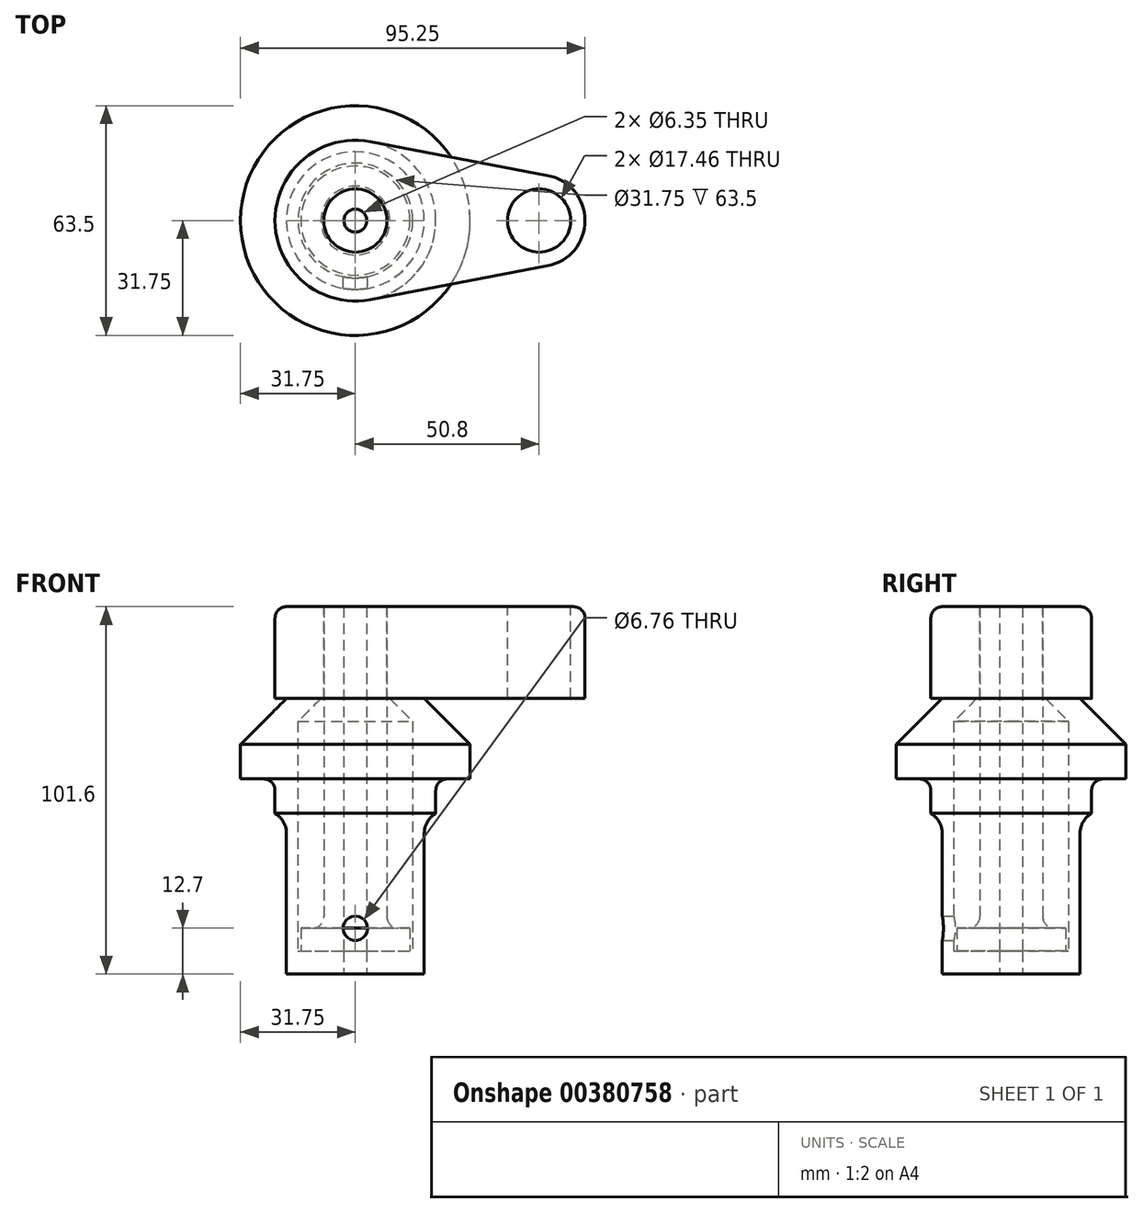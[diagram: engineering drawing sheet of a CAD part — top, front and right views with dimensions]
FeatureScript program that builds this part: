
annotation { "Feature Type Name" : "Feature", "Feature Type Description" : "" }
export const myFeature = defineFeature(function(context is Context, id is Id, definition is map)
    precondition{}
    {
        {
            var Q0;
            Q0=qCreatedBy(makeId("Front.planeOp"),FACE);
            var sketch = newSketch(context, id + "F0", { "sketchPlane" : qUnion([Q0])});
            skLineSegment(sketch, "E0", {"start": v(0, 0) * mm, "end": v(0, 76.2) * mm});
            skLineSegment(sketch, "E1", {"start": v(0, 76.2) * mm, "end": v(19.05, 76.2) * mm});
            skLineSegment(sketch, "E2", {"start": v(19.05, 76.2) * mm, "end": v(31.75, 63.5) * mm});
            skLineSegment(sketch, "E3", {"start": v(31.75, 63.5) * mm, "end": v(31.75, 53.98) * mm});
            skLineSegment(sketch, "E4", {"start": v(31.75, 53.98) * mm, "end": v(22.23, 53.98) * mm});
            skLineSegment(sketch, "E5", {"start": v(22.23, 53.98) * mm, "end": v(22.23, 44.45) * mm});
            skLineSegment(sketch, "E6", {"start": v(22.23, 44.45) * mm, "end": v(19.05, 44.45) * mm});
            skLineSegment(sketch, "E7", {"start": v(19.05, 44.45) * mm, "end": v(19.05, 0) * mm});
            skLineSegment(sketch, "E8", {"start": v(19.05, 0) * mm, "end": v(0, 0) * mm});
            skLineSegment(sketch, "E9", {"start": v(0, 6.35) * mm, "end": v(15.88, 6.35) * mm});
            skLineSegment(sketch, "E10", {"start": v(15.88, 6.35) * mm, "end": v(15.88, 69.85) * mm});
            skLineSegment(sketch, "E11", {"start": v(15.88, 69.85) * mm, "end": v(9.52, 76.2) * mm});
            skLineSegment(sketch, "E12", {"start": v(0, 76.2) * mm, "end": v(0, 87.9) * mm, "construction": true});
            skLineSegment(sketch, "E13", {"start": v(0, 76.2) * mm, "end": v(0, 101.6) * mm});
            skLineSegment(sketch, "E14", {"start": v(0, 101.6) * mm, "end": v(8.73, 101.6) * mm});
            skLineSegment(sketch, "E15", {"start": v(8.73, 101.6) * mm, "end": v(8.73, 12.7) * mm});
            skLineSegment(sketch, "E16", {"start": v(8.73, 12.7) * mm, "end": v(15.08, 12.7) * mm});
            skLineSegment(sketch, "E17", {"start": v(15.08, 12.7) * mm, "end": v(15.08, 6.35) * mm});
            skSolve(sketch);
        }
        {
            var Q0;
            {var subQ3=sQuery(id+"F0.wireOp",EDGE,"E2");Q0=makeQuery(id+"F0.imprint","IMPRINT",FACE,{"disambiguationData":[TD([[makeQuery(id+"F0.imprint","IMPRINT",EDGE,{"derivedFrom":subQ3}),-1.0]])]});}
            var Q1;
            Q1=sQuery(id+"F0.wireOp",EDGE,"E0");
            revolve(context, id + "F1", {"entities" : qUnion([Q0]), "axis" : qUnion([Q1]), "revolveType" : RevolveType.FULL});
        }
        {
            var Q0;
            {var subQ0=sQuery(id+"F0.wireOp",EDGE,"E13");Q0=makeQuery(id+"F0.imprint","IMPRINT",FACE,{"disambiguationData":[TD([[makeQuery(id+"F0.imprint","IMPRINT",EDGE,{"derivedFrom":subQ0}),-1.0]])]});}
            var Q1;
            {var subQ0=sQuery(id+"F0.wireOp",EDGE,"E16");Q1=makeQuery(id+"F0.imprint","IMPRINT",FACE,{"disambiguationData":[TD([[makeQuery(id+"F0.imprint","IMPRINT",EDGE,{"derivedFrom":subQ0}),-1.0]])]});}
            var Q2;
            Q2=sQuery(id+"F0.wireOp",EDGE,"E13");
            revolve(context, id + "F2", {"entities" : qUnion([Q0, Q1]), "axis" : qUnion([Q2]), "revolveType" : RevolveType.FULL});
        }
        {
            var Q0;
            Q0=makeQuery(id+"F2.opRevolve","SWEPT_FACE",FACE,{"disambiguationData":[OSD([sQuery(id+"F0.wireOp",EDGE,"E14")])]});
            var sketch = newSketch(context, id + "F3", { "sketchPlane" : qUnion([Q0])});
            skCircle(sketch, "E18", {"center": v(0, 0) * mm, "radius": 22.23 * mm});
            skCircle(sketch, "E19", {"center": v(50.8, 0) * mm, "radius": 12.7 * mm});
            skLineSegment(sketch, "E20", {"start": v(4.17, 21.83) * mm, "end": v(53.18, 12.47) * mm});
            skLineSegment(sketch, "E21", {"start": v(53.18, -12.47) * mm, "end": v(4.17, -21.83) * mm});
            skCircle(sketch, "E22.0", {"center": v(0, 0) * mm, "radius": 8.73 * mm});
            skCircle(sketch, "E23", {"center": v(50.8, 0) * mm, "radius": 8.73 * mm});
            skSolve(sketch);
        }
        {
            var Q0;
            Q0 = qSketchRegion(id + "F3", true);
            var Q1;
            Q1=makeQuery(id+"F1.opRevolve","SWEPT_FACE",FACE,{"disambiguationData":[OSD([sQuery(id+"F0.wireOp",EDGE,"E1")])]});
            extrude(context, id + "F4", {"entities" : qUnion([Q0]), "oppositeDirection" : true, "endBoundEntityFace" : qUnion([Q1]), "depth" : 25.4 * mm});
        }
        {
            var Q0;
            Q0=qCreatedBy(makeId("Front.planeOp"),FACE);
            var sketch = newSketch(context, id + "F5", { "sketchPlane" : qUnion([Q0])});
            skPoint(sketch, "E24", {"position": v(0, 12.7) * mm});
            skSolve(sketch);
        }
        {
            var Q0;
            Q0=sQuery(id+"F5.wireOp",VERTEX,"E24");
            var Q1;
            Q1=makeQuery(id+"F1.opRevolve","SWEPT_BODY",BODY,{"disambiguationData":[OSD([sQuery(id+"F0.wireOp",EDGE,"E0"),sQuery(id+"F0.wireOp",EDGE,"E1"),sQuery(id+"F0.wireOp",EDGE,"E2"),sQuery(id+"F0.wireOp",EDGE,"E3"),sQuery(id+"F0.wireOp",EDGE,"E4"),sQuery(id+"F0.wireOp",EDGE,"E5"),sQuery(id+"F0.wireOp",EDGE,"E6"),sQuery(id+"F0.wireOp",EDGE,"E7"),sQuery(id+"F0.wireOp",EDGE,"E8"),sQuery(id+"F0.wireOp",EDGE,"E9"),sQuery(id+"F0.wireOp",EDGE,"E10"),sQuery(id+"F0.wireOp",EDGE,"E11")])]});
            hole(context, id + "F6", {"style" : HoleStyle.SIMPLE, "endStyle" : HoleEndStyle.THROUGH, "oppositeDirection" : true, "standardTappedOrClearance" : lookupTablePath({ "standard" : "ANSI", "fit" : "Normal (ASME)", "size" : "1/4", "type" : "Clearance" }), "standardBlindInLast" : lookupTablePath({ "fit" : "Free", "standard" : "ANSI", "size" : "1/4", "type" : "Clearance" }), "holeDiameter" : 6.76 * mm, "isTappedThrough" : true, "tappedDepth" : 8.9 * mm, "tapClearance" : 3, "locations" : qUnion([Q0]), "scope" : qUnion([Q1])});
        }
        {
            var Q0;
            Q0=makeQuery(id+"F1.opRevolve","SWEPT_EDGE",EDGE,{"disambiguationData":[OSD([sQuery(id+"F0.wireOp",EDGE,"E4"),sQuery(id+"F0.wireOp",EDGE,"E5")])]});
            var Q1;
            Q1=makeQuery(id+"F4.opExtrude","CAP_EDGE",EDGE,{"disambiguationData":[OSD([sQuery(id+"F3.wireOp",EDGE,"E20")])],"isStart":true});
            var Q2;
            Q2=makeQuery(id+"F2.opRevolve","SWEPT_EDGE",EDGE,{"disambiguationData":[OSD([sQuery(id+"F0.wireOp",EDGE,"E15"),sQuery(id+"F0.wireOp",EDGE,"E16")])]});
            fillet(context, id + "F7", {"entities" : qUnion([Q0, Q1, Q2]), "radius" : 3.17 * mm, "tangentPropagation" : true, "allowEdgeOverflow" : false});
        }
        {
            var Q0;
            Q0=makeQuery(id+"F1.opRevolve","SWEPT_EDGE",EDGE,{"disambiguationData":[OSD([sQuery(id+"F0.wireOp",EDGE,"E6"),sQuery(id+"F0.wireOp",EDGE,"E7")])]});
            fillet(context, id + "F8", {"entities" : qUnion([Q0]), "radius" : 6.35 * mm, "tangentPropagation" : true, "allowEdgeOverflow" : false});
        }
        {
            var Q0;
            Q0=makeQuery(id+"F1.opRevolve","SWEPT_FACE",FACE,{"disambiguationData":[OSD([sQuery(id+"F0.wireOp",EDGE,"E8")])]});
            var sketch = newSketch(context, id + "F9", { "sketchPlane" : qUnion([Q0])});
            skCircle(sketch, "E25", {"center": v(0, 0) * mm, "radius": 3.18 * mm});
            skSolve(sketch);
        }
        {
            var Q0;
            Q0=makeQuery(id+"F9.imprint","IMPRINT",FACE,{"disambiguationData":[TD([[makeQuery(id+"F9.imprint","IMPRINT",EDGE,{"derivedFrom":sQuery(id+"F9.wireOp",EDGE,"E25")}),1.0]])]});
            extrude(context, id + "F10", {"entities" : qUnion([Q0]), "operationType" : NewBodyOperationType.REMOVE, "endBound" : BoundingType.THROUGH_ALL, "oppositeDirection" : true, "depth" : 25.4 * mm});
        }
    });
